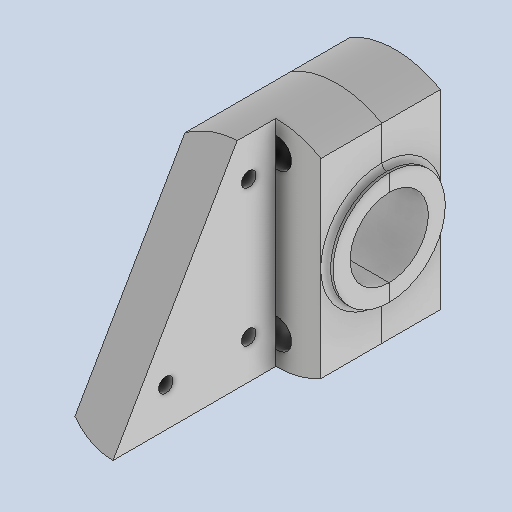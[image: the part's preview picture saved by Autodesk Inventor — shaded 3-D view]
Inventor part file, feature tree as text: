
AUTODESK INVENTOR PART (.ipt)
format: ipt  version: 2025.1 (Build 291241000, 241)  size: 356,864 bytes
history: native  units: mm
features: sketch x10, extrude x5, plane x4, hole x3, other x1, fillet x1, projected_geometry x1
ambient origin geometry x8: Origin, YZ Plane, XZ Plane, XY Plane, X Axis, Y Axis, Z Axis, Center Point
bodies: Volumenkörper1 (feature_tree)
feature tree (25):
  extrude  "Extrusion1"  Depth=18.5mm
  extrude  "Extrusion2"  Depth=18.5mm TaperAngle=0.0deg
  plane  "Arbeitsebene1"
  extrude  "Extrusion5"  Depth=45.8mm
  extrude  "Extrusion6"  Depth=12.0mm
  hole  "Bohrung4"  [1 undecoded]
  plane  "Arbeitsebene2"
  other  "Trennen2"
  sketch  "Skizze11"  dims[d46=1.5mm d47=0.0mm]
  plane  "Arbeitsebene3"
  fillet  "Rundung1"  Radius=12.0mm
  sketch  "Skizze17"  dims[d48=16.0mm d49=6.0mm d50=4.0mm d51=2.0mm d52=90.0deg d53=8.0mm d54=0.0mm d55=45.8mm]
  plane  "Arbeitsebene8"
  extrude  "Extrusion8"  Depth=2.0mm
  hole  "Bohrung11"  [1 undecoded]
  hole  "Bohrung12"  [1 undecoded]
  sketch  "Skizze1"  dims[d1=18.5mm d2=44.0mm]
  sketch  "Skizze2"  dims[d3=18.5mm d4=57.8mm d5=0.0mm]
  sketch  "Skizze8"  dims[d7=57.8mm d8=0.0mm d26=45.8mm]
  sketch  "Skizze9"  dims[d40=23.0mm d41=12.0mm]
  sketch  "Skizze10"  dims[d42=1.5mm d43=0.0mm d44=23.0mm d45=12.0mm]
  projected_geometry  "Projizierte Kontur1"
  sketch  "Skizze22"  dims[d67=16.0mm d68=32.0mm]
  sketch  "Skizze25"  dims[d76=0.0mm d91=1.0mm d112=10.39mm]
  sketch  "Skizze26"  dims[d113=6.0mm d121=19.0mm d123=10.0mm d124=0.0mm d125=9.5mm d143=60.0deg d144=10.8mm d145=14.0mm d146=17.0mm d147=14.0mm d148=3.0mm d149=7.0mm d150=5.0mm d151=2.0mm d152=90.0deg d153=8.0mm d154=20.594885mm d155=9.5mm d156=9.5mm d157=6.0mm d158=6.0mm d159=6.0mm d160=6.0mm d161=5.0mm d162=2.0mm d163=90.0deg d164=8.0mm d165=0.0mm]
note: 3 required parameter values undecoded (feature->parameter linkage not recoverable at this tier; creation-order binding heuristic only, values carry confidence <= 0.55)
